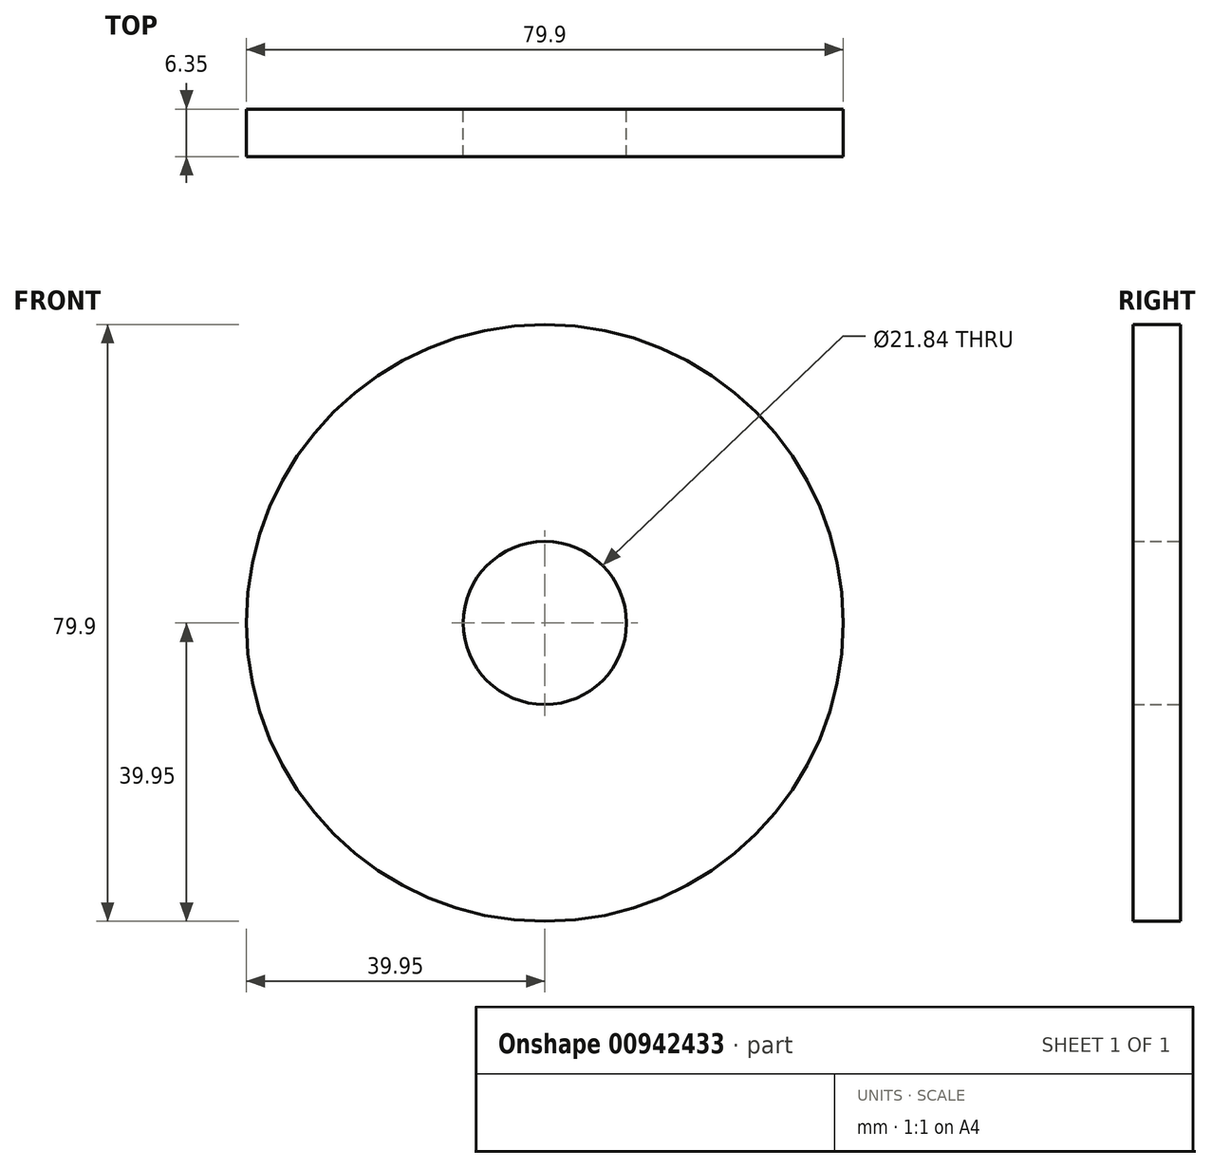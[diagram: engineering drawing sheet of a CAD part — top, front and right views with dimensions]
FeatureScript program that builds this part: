
annotation { "Feature Type Name" : "Feature", "Feature Type Description" : "" }
export const myFeature = defineFeature(function(context is Context, id is Id, definition is map)
    precondition{}
    {
        {
            var Q0;
            Q0=qCreatedBy(makeId("Front.planeOp"),FACE);
            var sketch = newSketch(context, id + "F0", { "sketchPlane" : qUnion([Q0])});
            skCircle(sketch, "E0", {"center": v(0, 0) * mm, "radius": 39.95 * mm});
            skArc(sketch, "E1", {"start": v(36.62, 0) * mm, "mid": v(31.72, 18.31) * mm, "end": v(18.31, 31.72) * mm});
            skCircle(sketch, "E2", {"center": v(0, 0) * mm, "radius": 10.92 * mm});
            skArc(sketch, "E3", {"start": v(14.83, 0) * mm, "mid": v(12.85, 7.42) * mm, "end": v(7.42, 12.85) * mm});
            skLineSegment(sketch, "E4", {"start": v(-36.62, 0) * mm, "end": v(-14.83, 0) * mm});
            skLineSegment(sketch, "E5.1.0", {"start": v(-18.31, -31.72) * mm, "end": v(-7.42, -12.85) * mm});
            skLineSegment(sketch, "E5.2.0", {"start": v(18.31, -31.72) * mm, "end": v(7.42, -12.85) * mm});
            skLineSegment(sketch, "E5.3.0", {"start": v(36.62, 0) * mm, "end": v(14.83, 0) * mm});
            skLineSegment(sketch, "E5.4.0", {"start": v(18.31, 31.72) * mm, "end": v(7.42, 12.85) * mm});
            skLineSegment(sketch, "E5.5.0", {"start": v(-18.31, 31.72) * mm, "end": v(-7.42, 12.85) * mm});
            skArc(sketch, "E6.trimOffspring", {"start": v(-7.42, 12.85) * mm, "mid": v(-12.85, 7.42) * mm, "end": v(-14.83, 0) * mm});
            skArc(sketch, "E7.trimOffspring", {"start": v(-18.31, 31.72) * mm, "mid": v(-31.72, 18.31) * mm, "end": v(-36.62, 0) * mm});
            skArc(sketch, "E8.trimOffspring", {"start": v(-7.42, -12.85) * mm, "mid": v(0, -14.83) * mm, "end": v(7.42, -12.85) * mm});
            skArc(sketch, "E9.trimOffspring", {"start": v(-18.31, -31.72) * mm, "mid": v(0, -36.62) * mm, "end": v(18.31, -31.72) * mm});
            skSolve(sketch);
        }
        {
            var Q0;
            Q0=makeQuery(id+"F0.imprint","IMPRINT",FACE,{"disambiguationData":[TD([[makeQuery(id+"F0.imprint","IMPRINT",EDGE,{"derivedFrom":sQuery(id+"F0.wireOp",EDGE,"E0")}),1.0]])]});
            var Q1;
            {var subQ0=sQuery(id+"F0.wireOp",EDGE,"E5.3.0");Q1=makeQuery(id+"F0.imprint","IMPRINT",FACE,{"disambiguationData":[TD([[makeQuery(id+"F0.imprint","IMPRINT",EDGE,{"derivedFrom":subQ0}),-1.0]])]});}
            var Q2;
            {var subQ0=sQuery(id+"F0.wireOp",EDGE,"E5.1.0");Q2=makeQuery(id+"F0.imprint","IMPRINT",FACE,{"disambiguationData":[TD([[makeQuery(id+"F0.imprint","IMPRINT",EDGE,{"derivedFrom":subQ0}),-1.0]])]});}
            var Q3;
            {var subQ0=sQuery(id+"F0.wireOp",EDGE,"E4");Q3=makeQuery(id+"F0.imprint","IMPRINT",FACE,{"disambiguationData":[TD([[makeQuery(id+"F0.imprint","IMPRINT",EDGE,{"derivedFrom":subQ0}),1.0]])]});}
            var Q4;
            Q4=makeQuery(id+"F0.imprint","IMPRINT",FACE,{"disambiguationData":[TD([[makeQuery(id+"F0.imprint","IMPRINT",EDGE,{"derivedFrom":sQuery(id+"F0.wireOp",EDGE,"E2")}),-1.0]])]});
            extrude(context, id + "F1", {"entities" : qUnion([Q0, Q1, Q2, Q3, Q4]), "depth" : 6.35 * mm, "offsetDistance" : 25.4 * mm});
        }
    });
